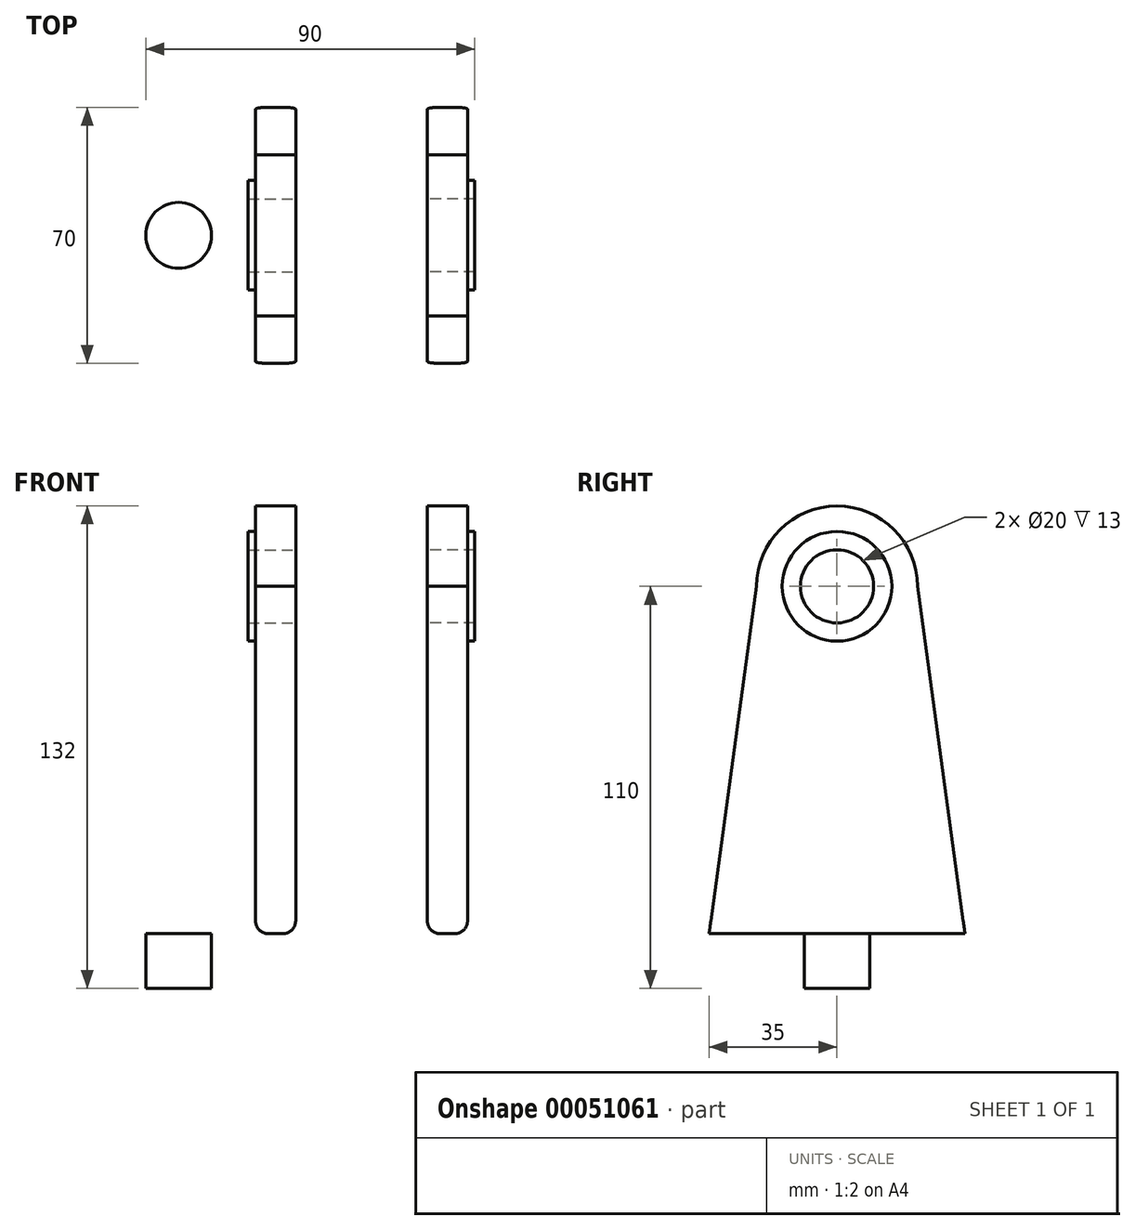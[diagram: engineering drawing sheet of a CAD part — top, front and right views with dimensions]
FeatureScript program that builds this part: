
annotation { "Feature Type Name" : "Feature", "Feature Type Description" : "" }
export const myFeature = defineFeature(function(context is Context, id is Id, definition is map)
    precondition{}
    {
        {
            var Q0;
            Q0=qCreatedBy(makeId("Top.planeOp"),FACE);
            var sketch = newSketch(context, id + "F0", { "sketchPlane" : qUnion([Q0])});
            skLineSegment(sketch, "E0", {"start": v(-84.18, 0) * mm, "end": v(83.86, 0) * mm, "construction": true});
            skLineSegment(sketch, "E1", {"start": v(0, -37.82) * mm, "end": v(0, 39.4) * mm, "construction": true});
            skArc(sketch, "E2", {"start": v(-59, 0) * mm, "mid": v(-50, 9) * mm, "end": v(-41, 0) * mm});
            skArc(sketch, "E3", {"start": v(41, 0) * mm, "mid": v(50, 9) * mm, "end": v(59, 0) * mm});
            skLineSegment(sketch, "E4", {"start": v(-70, 0) * mm, "end": v(-70, 30) * mm});
            skArc(sketch, "E5", {"start": v(-70, 30) * mm, "mid": v(-68.82, 33.22) * mm, "end": v(-65.84, 34.93) * mm});
            skLineSegment(sketch, "E6", {"start": v(-65.84, 34.93) * mm, "end": v(64.16, 34.93) * mm});
            skArc(sketch, "E7", {"start": v(64.16, 34.93) * mm, "mid": v(67.67, 33.49) * mm, "end": v(69.15, 30) * mm});
            skLineSegment(sketch, "E8", {"start": v(69.15, 30) * mm, "end": v(69.15, 0) * mm});
            skArc(sketch, "E9.MirrorCS", {"start": v(-59, 0) * mm, "mid": v(-50, -9) * mm, "end": v(-41, 0) * mm});
            skLineSegment(sketch, "E10.MirrorCS", {"start": v(-70, 0) * mm, "end": v(-70, -30) * mm});
            skArc(sketch, "E11.MirrorCS", {"start": v(-70, -30) * mm, "mid": v(-68.82, -33.22) * mm, "end": v(-65.84, -34.93) * mm});
            skLineSegment(sketch, "E12.MirrorCS", {"start": v(-65.84, -34.93) * mm, "end": v(64.16, -34.93) * mm});
            skArc(sketch, "E13.MirrorCS", {"start": v(41, 0) * mm, "mid": v(50, -9) * mm, "end": v(59, 0) * mm});
            skLineSegment(sketch, "E14.MirrorCS", {"start": v(69.15, -30) * mm, "end": v(69.15, 0) * mm});
            skArc(sketch, "E15.MirrorCS", {"start": v(64.16, -34.93) * mm, "mid": v(67.67, -33.49) * mm, "end": v(69.15, -30) * mm});
            skSolve(sketch);
        }
        {
            var Q0;
            Q0=qCreatedBy(makeId("Right.planeOp"),FACE);
            cPlane(context, id + "F1", {"entities" : qUnion([Q0]), "cplaneType" : CPlaneType.OFFSET, "offset" : 18 * mm, "oppositeDirection" : true, "width" : 150 * mm, "height" : 150 * mm});
        }
        {
            var Q0;
            Q0=qCreatedBy(id+"F1.planeOp",FACE);
            var sketch = newSketch(context, id + "F2", { "sketchPlane" : qUnion([Q0])});
            skLineSegment(sketch, "E16", {"start": v(0, 0) * mm, "end": v(0, 95) * mm});
            skArc(sketch, "E17", {"start": v(22, 95) * mm, "mid": v(0, 117) * mm, "end": v(-22, 95) * mm});
            skArc(sketch, "E18", {"start": v(15, 95) * mm, "mid": v(0, 110) * mm, "end": v(-15, 95) * mm});
            skArc(sketch, "E19", {"start": v(10, 95) * mm, "mid": v(0, 105) * mm, "end": v(-10, 95) * mm});
            skArc(sketch, "E20.MirrorCS", {"start": v(15, 95) * mm, "mid": v(0, 80) * mm, "end": v(-15, 95) * mm});
            skArc(sketch, "E21.MirrorCS", {"start": v(10, 95) * mm, "mid": v(0, 85) * mm, "end": v(-10, 95) * mm});
            skLineSegment(sketch, "E22", {"start": v(0, 0) * mm, "end": v(-35, 0) * mm});
            skLineSegment(sketch, "E23", {"start": v(0, 0) * mm, "end": v(35, 0) * mm});
            skLineSegment(sketch, "E24", {"start": v(22, 95) * mm, "end": v(35, 0) * mm});
            skLineSegment(sketch, "E25", {"start": v(-22, 95) * mm, "end": v(-35, 0) * mm});
            skSolve(sketch);
        }
        {
            var Q0;
            Q0=qCreatedBy(makeId("Right.planeOp"),FACE);
            cPlane(context, id + "F3", {"entities" : qUnion([Q0]), "cplaneType" : CPlaneType.OFFSET, "offset" : 18 * mm, "width" : 150 * mm, "height" : 150 * mm});
        }
        {
            var Q0;
            Q0=qCreatedBy(id+"F3.planeOp",FACE);
            var sketch = newSketch(context, id + "F4", { "sketchPlane" : qUnion([Q0])});
            skLineSegment(sketch, "E26.0", {"start": v(-22, 95) * mm, "end": v(-35, 0) * mm});
            skLineSegment(sketch, "E26.1", {"start": v(0, 0) * mm, "end": v(0, 95) * mm});
            skLineSegment(sketch, "E26.2", {"start": v(22, 95) * mm, "end": v(35, 0) * mm});
            skArc(sketch, "E26.3", {"start": v(22, 95) * mm, "mid": v(0, 117) * mm, "end": v(-22, 95) * mm});
            skArc(sketch, "E26.4", {"start": v(15, 95) * mm, "mid": v(0, 110) * mm, "end": v(-15, 95) * mm});
            skArc(sketch, "E26.5", {"start": v(10, 95) * mm, "mid": v(0, 105) * mm, "end": v(-10, 95) * mm});
            skArc(sketch, "E26.6", {"start": v(10, 95) * mm, "mid": v(0, 85) * mm, "end": v(-10, 95) * mm});
            skArc(sketch, "E26.7", {"start": v(15, 95) * mm, "mid": v(0, 80) * mm, "end": v(-15, 95) * mm});
            skLineSegment(sketch, "E27.0", {"start": v(0, 0) * mm, "end": v(-35, 0) * mm});
            skLineSegment(sketch, "E27.1", {"start": v(0, 0) * mm, "end": v(35, 0) * mm});
            skSolve(sketch);
        }
        {
            var Q0;
            Q0=makeQuery(id+"F0.imprint","IMPRINT",FACE,{"disambiguationData":[TD([[makeQuery(id+"F0.imprint","IMPRINT",EDGE,{"derivedFrom":sQuery(id+"F0.wireOp",EDGE,"E2")}),1.0]])]});
            extrude(context, id + "F5", {"entities" : qUnion([Q0]), "oppositeDirection" : true, "depth" : 15 * mm});
        }
        {
            var Q0;
            Q0=makeQuery(id+"F2.imprint","IMPRINT",FACE,{"disambiguationData":[TD([[makeQuery(id+"F2.imprint","IMPRINT",EDGE,{"derivedFrom":sQuery(id+"F2.wireOp",EDGE,"E17")}),1.0]])]});
            extrude(context, id + "F6", {"entities" : qUnion([Q0]), "operationType" : NewBodyOperationType.ADD, "oppositeDirection" : true, "depth" : 11 * mm});
        }
        {
            var Q0;
            Q0=makeQuery(id+"F4.imprint","IMPRINT",FACE,{"disambiguationData":[TD([[makeQuery(id+"F4.imprint","IMPRINT",EDGE,{"derivedFrom":sQuery(id+"F4.wireOp",EDGE,"E26.0")}),1.0]])]});
            extrude(context, id + "F7", {"entities" : qUnion([Q0]), "operationType" : NewBodyOperationType.ADD, "depth" : 11 * mm});
        }
        {
            var Q0;
            {var subQ1=sQuery(id+"F2.wireOp",EDGE,"E18");Q0=makeQuery(id+"F2.imprint","IMPRINT",FACE,{"disambiguationData":[TD([[makeQuery(id+"F2.imprint","IMPRINT",EDGE,{"derivedFrom":subQ1}),1.0]])]});}
            extrude(context, id + "F8", {"entities" : qUnion([Q0]), "operationType" : NewBodyOperationType.ADD, "oppositeDirection" : true, "depth" : 13 * mm});
        }
        {
            var Q0;
            {var subQ3=sQuery(id+"F4.wireOp",EDGE,"E26.4");Q0=makeQuery(id+"F4.imprint","IMPRINT",FACE,{"disambiguationData":[TD([[makeQuery(id+"F4.imprint","IMPRINT",EDGE,{"derivedFrom":subQ3}),1.0]])]});}
            extrude(context, id + "F9", {"entities" : qUnion([Q0]), "operationType" : NewBodyOperationType.ADD, "depth" : 13 * mm});
        }
        {
            var Q0;
            {var subQ0=sQuery(id+"F2.wireOp",EDGE,"E23");var subQ1=sQuery(id+"F2.wireOp",EDGE,"E22");var subQ2=sQuery(id+"F0.wireOp",EDGE,"E12.MirrorCS");var subQ3=sQuery(id+"F0.wireOp",EDGE,"E6");Q0=makeQuery(id+"F6.boolean.opBoolean","SPLIT",EDGE,{"disambiguationData":[TD([makeQuery(id+"F5.opExtrude","CAP_FACE",FACE,{"disambiguationData":[OSD([sQuery(id+"F0.wireOp",EDGE,"E2"),sQuery(id+"F0.wireOp",EDGE,"E3"),sQuery(id+"F0.wireOp",EDGE,"E4"),sQuery(id+"F0.wireOp",EDGE,"E5"),subQ3,sQuery(id+"F0.wireOp",EDGE,"E7"),sQuery(id+"F0.wireOp",EDGE,"E8"),sQuery(id+"F0.wireOp",EDGE,"E9.MirrorCS"),sQuery(id+"F0.wireOp",EDGE,"E10.MirrorCS"),sQuery(id+"F0.wireOp",EDGE,"E11.MirrorCS"),subQ2,sQuery(id+"F0.wireOp",EDGE,"E13.MirrorCS"),sQuery(id+"F0.wireOp",EDGE,"E14.MirrorCS"),sQuery(id+"F0.wireOp",EDGE,"E15.MirrorCS")])],"isStart":true}),makeQuery(id+"F5.opExtrude","SWEPT_FACE",FACE,{"disambiguationData":[OSD([subQ3])]}),makeQuery(id+"F5.opExtrude","SWEPT_FACE",FACE,{"disambiguationData":[OSD([subQ2])]}),makeQuery(id+"F6.opExtrude","CAP_FACE",FACE,{"disambiguationData":[OSD([sQuery(id+"F2.wireOp",EDGE,"E17"),sQuery(id+"F2.wireOp",EDGE,"E18"),sQuery(id+"F2.wireOp",EDGE,"E20.MirrorCS"),subQ1,subQ0,sQuery(id+"F2.wireOp",EDGE,"E24"),sQuery(id+"F2.wireOp",EDGE,"E25")])],"isStart":false}),makeQuery(id+"F6.opExtrude","SWEPT_FACE",FACE,{"disambiguationData":[OSD([subQ1,subQ0])]})])],"derivedFrom":makeQuery(id+"F6.opExtrude","CAP_EDGE",EDGE,{"disambiguationData":[OSD([subQ1,subQ0])],"isStart":false})});}
            var Q1;
            {var subQ0=sQuery(id+"F0.wireOp",EDGE,"E12.MirrorCS");var subQ1=sQuery(id+"F0.wireOp",EDGE,"E6");var subQ2=sQuery(id+"F2.wireOp",EDGE,"E23");var subQ3=sQuery(id+"F2.wireOp",EDGE,"E22");Q1=makeQuery(id+"F6.boolean.opBoolean","SPLIT",EDGE,{"disambiguationData":[TD([makeQuery(id+"F5.opExtrude","CAP_FACE",FACE,{"disambiguationData":[OSD([sQuery(id+"F0.wireOp",EDGE,"E2"),sQuery(id+"F0.wireOp",EDGE,"E3"),sQuery(id+"F0.wireOp",EDGE,"E4"),sQuery(id+"F0.wireOp",EDGE,"E5"),subQ1,sQuery(id+"F0.wireOp",EDGE,"E7"),sQuery(id+"F0.wireOp",EDGE,"E8"),sQuery(id+"F0.wireOp",EDGE,"E9.MirrorCS"),sQuery(id+"F0.wireOp",EDGE,"E10.MirrorCS"),sQuery(id+"F0.wireOp",EDGE,"E11.MirrorCS"),subQ0,sQuery(id+"F0.wireOp",EDGE,"E13.MirrorCS"),sQuery(id+"F0.wireOp",EDGE,"E14.MirrorCS"),sQuery(id+"F0.wireOp",EDGE,"E15.MirrorCS")])],"isStart":true}),makeQuery(id+"F5.opExtrude","SWEPT_FACE",FACE,{"disambiguationData":[OSD([subQ1])]}),makeQuery(id+"F5.opExtrude","SWEPT_FACE",FACE,{"disambiguationData":[OSD([subQ0])]}),makeQuery(id+"F6.opExtrude","CAP_FACE",FACE,{"disambiguationData":[OSD([sQuery(id+"F2.wireOp",EDGE,"E17"),sQuery(id+"F2.wireOp",EDGE,"E18"),sQuery(id+"F2.wireOp",EDGE,"E20.MirrorCS"),subQ3,subQ2,sQuery(id+"F2.wireOp",EDGE,"E24"),sQuery(id+"F2.wireOp",EDGE,"E25")])],"isStart":true}),makeQuery(id+"F6.opExtrude","SWEPT_FACE",FACE,{"disambiguationData":[OSD([subQ3,subQ2])]})])],"derivedFrom":makeQuery(id+"F6.opExtrude","CAP_EDGE",EDGE,{"disambiguationData":[OSD([subQ3,subQ2])],"isStart":true})});}
            var Q2;
            {var subQ0=sQuery(id+"F4.wireOp",EDGE,"E27.1");var subQ1=sQuery(id+"F4.wireOp",EDGE,"E27.0");var subQ2=sQuery(id+"F0.wireOp",EDGE,"E12.MirrorCS");var subQ3=sQuery(id+"F0.wireOp",EDGE,"E6");Q2=makeQuery(id+"F7.boolean.opBoolean","SPLIT",EDGE,{"disambiguationData":[TD([makeQuery(id+"F5.opExtrude","CAP_FACE",FACE,{"disambiguationData":[OSD([sQuery(id+"F0.wireOp",EDGE,"E2"),sQuery(id+"F0.wireOp",EDGE,"E3"),sQuery(id+"F0.wireOp",EDGE,"E4"),sQuery(id+"F0.wireOp",EDGE,"E5"),subQ3,sQuery(id+"F0.wireOp",EDGE,"E7"),sQuery(id+"F0.wireOp",EDGE,"E8"),sQuery(id+"F0.wireOp",EDGE,"E9.MirrorCS"),sQuery(id+"F0.wireOp",EDGE,"E10.MirrorCS"),sQuery(id+"F0.wireOp",EDGE,"E11.MirrorCS"),subQ2,sQuery(id+"F0.wireOp",EDGE,"E13.MirrorCS"),sQuery(id+"F0.wireOp",EDGE,"E14.MirrorCS"),sQuery(id+"F0.wireOp",EDGE,"E15.MirrorCS")])],"isStart":true}),makeQuery(id+"F5.opExtrude","SWEPT_FACE",FACE,{"disambiguationData":[OSD([subQ3])]}),makeQuery(id+"F5.opExtrude","SWEPT_FACE",FACE,{"disambiguationData":[OSD([subQ2])]}),makeQuery(id+"F7.opExtrude","CAP_FACE",FACE,{"disambiguationData":[OSD([sQuery(id+"F4.wireOp",EDGE,"E26.0"),sQuery(id+"F4.wireOp",EDGE,"E26.2"),sQuery(id+"F4.wireOp",EDGE,"E26.3"),sQuery(id+"F4.wireOp",EDGE,"E26.4"),sQuery(id+"F4.wireOp",EDGE,"E26.7"),subQ1,subQ0])],"isStart":true}),makeQuery(id+"F7.opExtrude","SWEPT_FACE",FACE,{"disambiguationData":[OSD([subQ1,subQ0])]})])],"derivedFrom":makeQuery(id+"F7.opExtrude","CAP_EDGE",EDGE,{"disambiguationData":[OSD([subQ1,subQ0])],"isStart":true})});}
            var Q3;
            {var subQ0=sQuery(id+"F4.wireOp",EDGE,"E27.1");var subQ1=sQuery(id+"F4.wireOp",EDGE,"E27.0");var subQ2=sQuery(id+"F0.wireOp",EDGE,"E12.MirrorCS");var subQ3=sQuery(id+"F0.wireOp",EDGE,"E6");Q3=makeQuery(id+"F7.boolean.opBoolean","SPLIT",EDGE,{"disambiguationData":[TD([makeQuery(id+"F5.opExtrude","CAP_FACE",FACE,{"disambiguationData":[OSD([sQuery(id+"F0.wireOp",EDGE,"E2"),sQuery(id+"F0.wireOp",EDGE,"E3"),sQuery(id+"F0.wireOp",EDGE,"E4"),sQuery(id+"F0.wireOp",EDGE,"E5"),subQ3,sQuery(id+"F0.wireOp",EDGE,"E7"),sQuery(id+"F0.wireOp",EDGE,"E8"),sQuery(id+"F0.wireOp",EDGE,"E9.MirrorCS"),sQuery(id+"F0.wireOp",EDGE,"E10.MirrorCS"),sQuery(id+"F0.wireOp",EDGE,"E11.MirrorCS"),subQ2,sQuery(id+"F0.wireOp",EDGE,"E13.MirrorCS"),sQuery(id+"F0.wireOp",EDGE,"E14.MirrorCS"),sQuery(id+"F0.wireOp",EDGE,"E15.MirrorCS")])],"isStart":true}),makeQuery(id+"F5.opExtrude","SWEPT_FACE",FACE,{"disambiguationData":[OSD([subQ3])]}),makeQuery(id+"F5.opExtrude","SWEPT_FACE",FACE,{"disambiguationData":[OSD([subQ2])]}),makeQuery(id+"F7.opExtrude","CAP_FACE",FACE,{"disambiguationData":[OSD([sQuery(id+"F4.wireOp",EDGE,"E26.0"),sQuery(id+"F4.wireOp",EDGE,"E26.2"),sQuery(id+"F4.wireOp",EDGE,"E26.3"),sQuery(id+"F4.wireOp",EDGE,"E26.4"),sQuery(id+"F4.wireOp",EDGE,"E26.7"),subQ1,subQ0])],"isStart":false}),makeQuery(id+"F7.opExtrude","SWEPT_FACE",FACE,{"disambiguationData":[OSD([subQ1,subQ0])]})])],"derivedFrom":makeQuery(id+"F7.opExtrude","CAP_EDGE",EDGE,{"disambiguationData":[OSD([subQ1,subQ0])],"isStart":false})});}
            fillet(context, id + "F10", {"entities" : qUnion([Q0, Q1, Q2, Q3]), "radius" : 3.5 * mm, "tangentPropagation" : true, "allowEdgeOverflow" : false});
        }
    });
